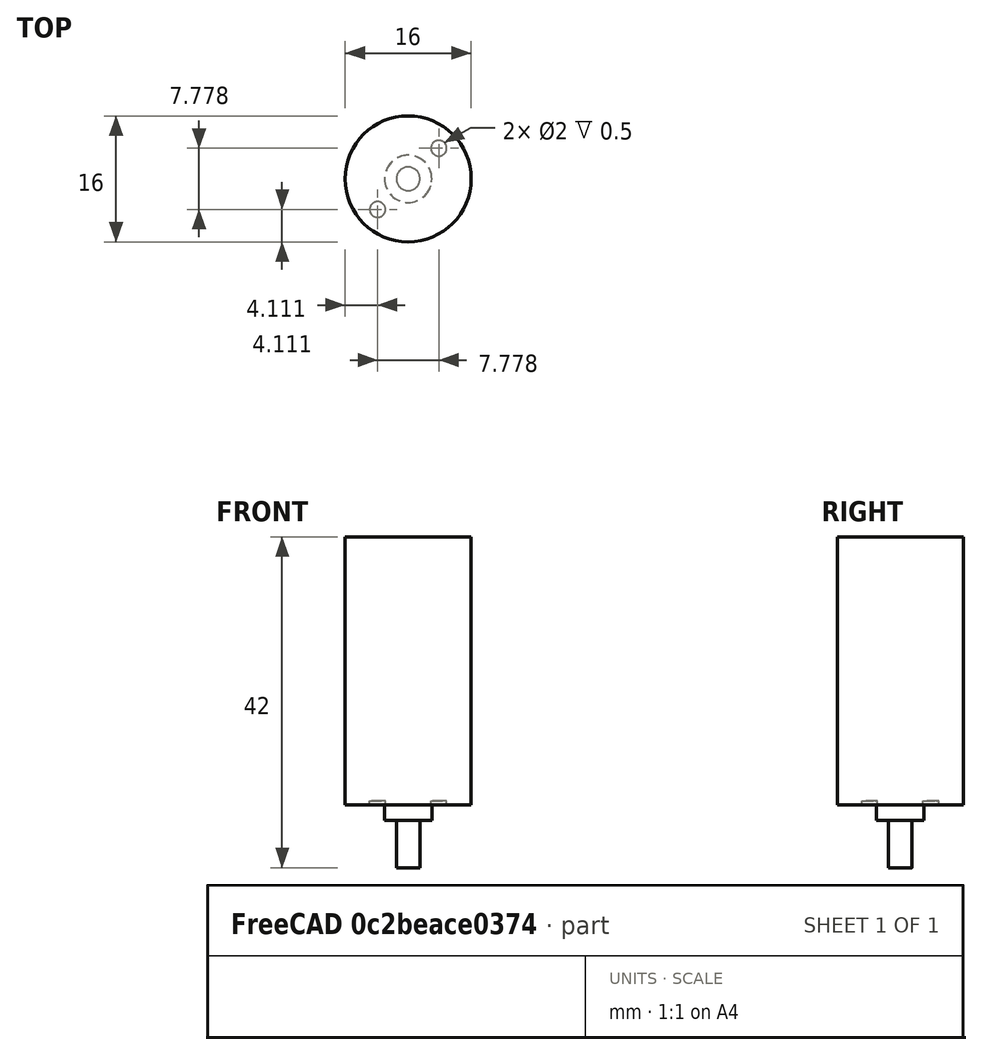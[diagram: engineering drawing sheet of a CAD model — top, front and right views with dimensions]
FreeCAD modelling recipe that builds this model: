
FCSTD DOCUMENT
Label: 16mm_gear_motor
License: CC-BY 3.0
LicenseURL: http://creativecommons.org/licenses/by/3.0/
objects: Part::Cylinder×5, Part::Cut×2, Part::MultiFuse×1
note: 8 computed .brp shape members not serialized (recipe doc carries the construction recipe); baked Part::Feature solids carry a one-line shape summary decoded from their .brp

FEATURE [Part::Cylinder] Cylinder  label="motor_body"
  Angle = 360
  Height = 34
  Radius = 8
FEATURE [Part::Cylinder] Cylinder001  label="motor_shaft"
  Angle = 360
  Height = 8
  Placement = pos=(0,0,-8) rot=(0,0,1;0rad)
  Radius = 1.5
FEATURE [Part::Cylinder] Cylinder002  label="bearing"
  Angle = 360
  Height = 2.5
  Placement = pos=(0,0,-2) rot=(0,0,1;0rad)
  Radius = 3
FEATURE [Part::Cylinder] Cylinder003
  Angle = 360
  Height = 8.5
  Placement = pos=(5.5,0,-8) rot=(0,0,1;0rad)
  Radius = 1
FEATURE [Part::Cylinder] Cylinder004
  Angle = 360
  Height = 8.5
  Placement = pos=(-5.5,0,-8) rot=(0,0,1;0rad)
  Radius = 1
FEATURE [Part::Cut] Cut
  Base = -> Cylinder
  Tool = -> Cylinder003
FEATURE [Part::Cut] Cut001
  Base = -> Cut
  Tool = -> Cylinder004
FEATURE [Part::MultiFuse] Fusion  label="16mmGearMotor"
  Placement = pos=(0,0,0) rot=(0,0,1;0.785397rad)
  Shapes = -> [Cylinder001,Cylinder002,Cut001]
